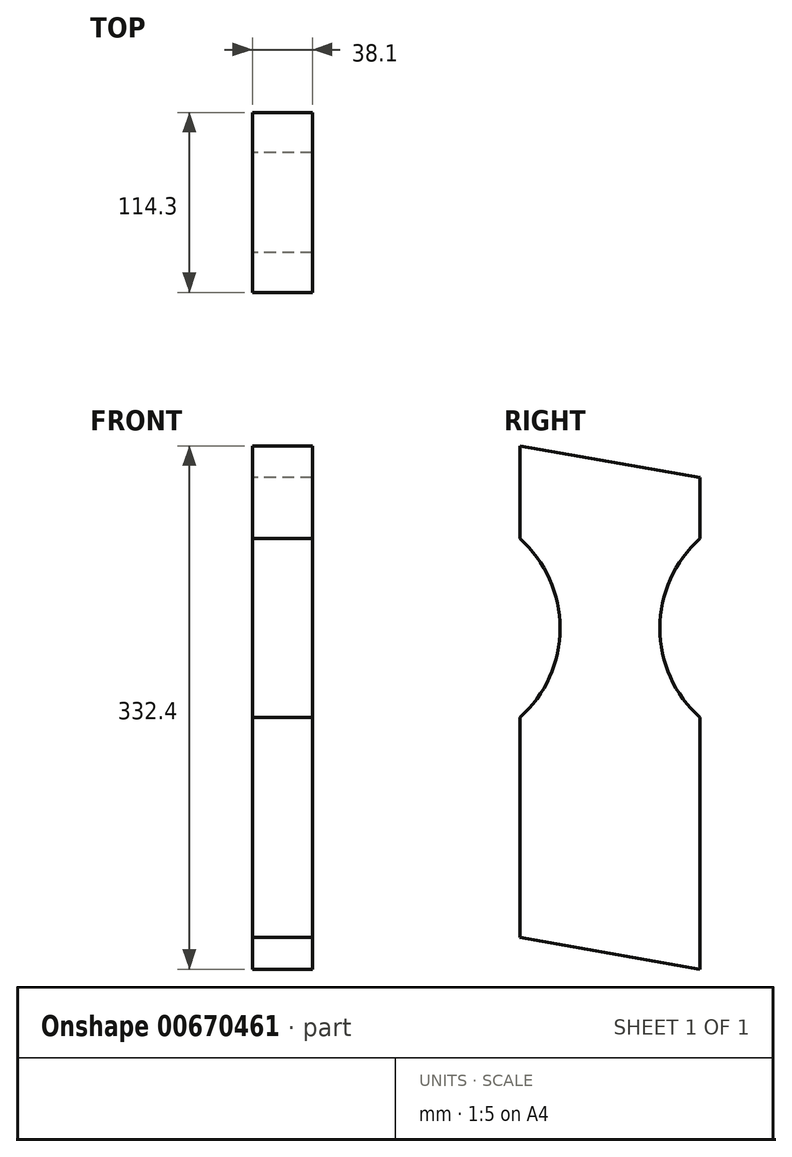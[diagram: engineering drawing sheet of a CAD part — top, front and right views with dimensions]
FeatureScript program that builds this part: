
annotation { "Feature Type Name" : "Feature", "Feature Type Description" : "" }
export const myFeature = defineFeature(function(context is Context, id is Id, definition is map)
    precondition{}
    {
        {
            var Q0;
            Q0=qCreatedBy(makeId("Right.planeOp"),FACE);
            var sketch = newSketch(context, id + "F0", { "sketchPlane" : qUnion([Q0])});
            skLineSegment(sketch, "E0.bottom", {"start": v(0, 0) * mm, "end": v(-114.3, 0) * mm, "construction": true});
            skLineSegment(sketch, "E0.top", {"start": v(0, 292.1) * mm, "end": v(-114.3, 292.1) * mm, "construction": true});
            skLineSegment(sketch, "E0.left", {"start": v(0, -20.15) * mm, "end": v(0, 139.7) * mm});
            skLineSegment(sketch, "E0.right", {"start": v(-114.3, 0) * mm, "end": v(-114.3, 139.7) * mm});
            skArc(sketch, "E1", {"start": v(-114.3, 139.7) * mm, "mid": v(-88.9, 196.5) * mm, "end": v(-114.3, 253.3) * mm});
            skLineSegment(sketch, "E2", {"start": v(-57.15, 292.1) * mm, "end": v(-57.15, 0) * mm, "construction": true});
            skArc(sketch, "E3.MirrorCS", {"start": v(0, 139.7) * mm, "mid": v(-25.4, 196.5) * mm, "end": v(0, 253.3) * mm});
            skLineSegment(sketch, "E4.trimOffspring", {"start": v(-114.3, 253.3) * mm, "end": v(-114.3, 312.25) * mm});
            skLineSegment(sketch, "E5.trimOffspring", {"start": v(0, 253.3) * mm, "end": v(0, 292.1) * mm});
            skLineSegment(sketch, "E6", {"start": v(0, 292.1) * mm, "end": v(-114.3, 312.25) * mm});
            skLineSegment(sketch, "E7", {"start": v(-114.3, 0) * mm, "end": v(0, -20.15) * mm});
            skLineSegment(sketch, "E8", {"start": v(-114.3, 312.25) * mm, "end": v(-114.3, 292.1) * mm, "construction": true});
            skLineSegment(sketch, "E9", {"start": v(0, 0) * mm, "end": v(0, -20.15) * mm, "construction": true});
            skSolve(sketch);
        }
        {
            var Q0;
            Q0=makeQuery(id+"F0.imprint","IMPRINT",FACE,{"disambiguationData":[TD([[makeQuery(id+"F0.imprint","IMPRINT",EDGE,{"derivedFrom":sQuery(id+"F0.wireOp",EDGE,"E0.left")}),1.0]])]});
            extrude(context, id + "F1", {"entities" : qUnion([Q0]), "depth" : 38.1 * mm, "offsetDistance" : 25.4 * mm});
        }
    });
